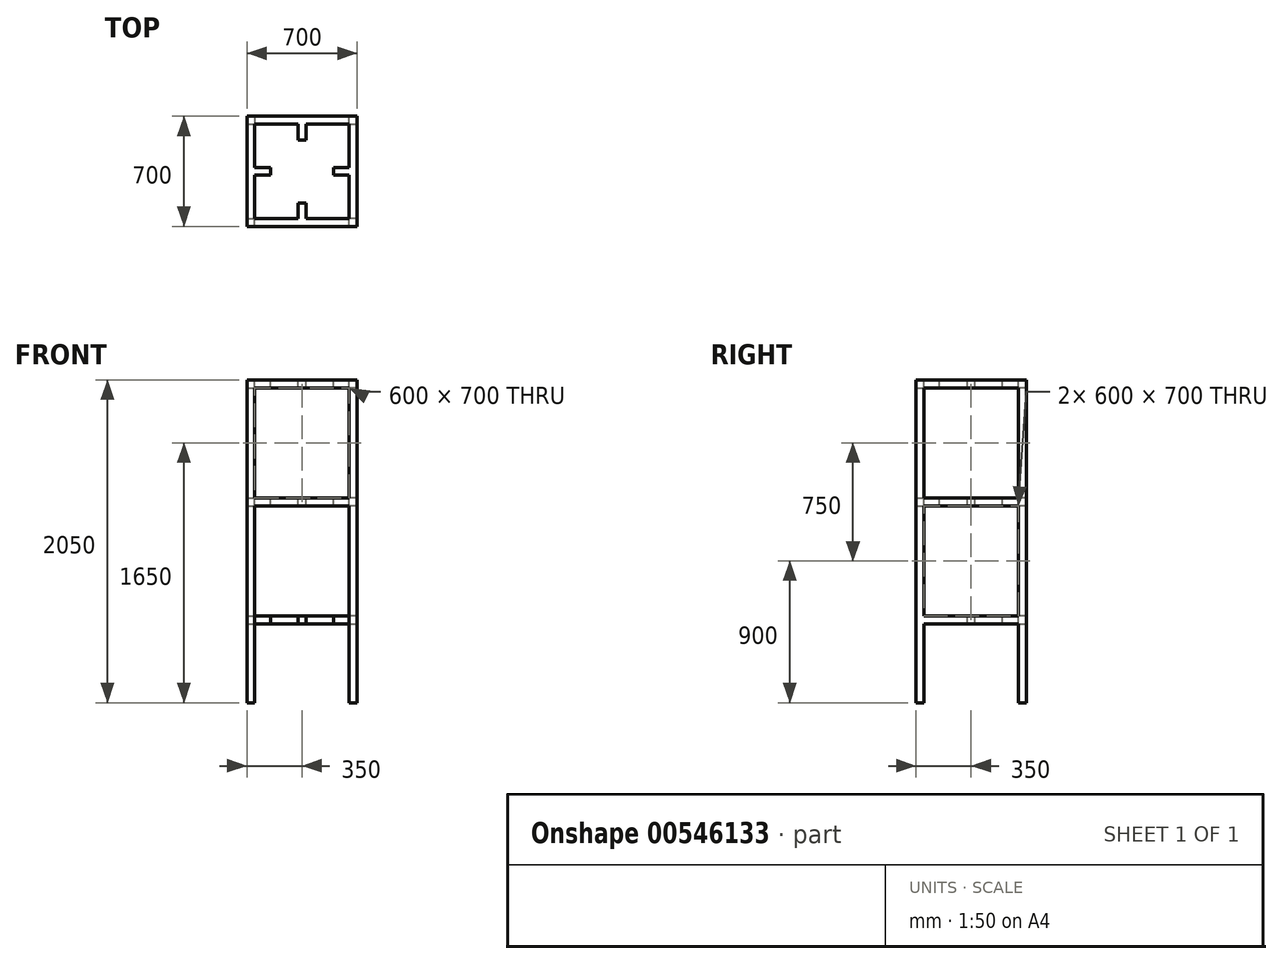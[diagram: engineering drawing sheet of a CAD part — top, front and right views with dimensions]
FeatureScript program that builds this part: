
annotation { "Feature Type Name" : "Feature", "Feature Type Description" : "" }
export const myFeature = defineFeature(function(context is Context, id is Id, definition is map)
    precondition{}
    {
        {
            var Q0;
            Q0=qCreatedBy(makeId("Top.planeOp"),FACE);
            var sketch = newSketch(context, id + "F0", { "sketchPlane" : qUnion([Q0])});
            skLineSegment(sketch, "E0.bottom", {"start": v(350, -350) * mm, "end": v(-350, -350) * mm});
            skLineSegment(sketch, "E0.top", {"start": v(350, 350) * mm, "end": v(-350, 350) * mm});
            skLineSegment(sketch, "E0.left", {"start": v(350, -350) * mm, "end": v(350, 350) * mm});
            skLineSegment(sketch, "E0.right", {"start": v(-350, -350) * mm, "end": v(-350, 350) * mm});
            skPoint(sketch, "E0.middle", {"position": v(0, 0) * mm});
            skLineSegment(sketch, "E1.bottom", {"start": v(300, -300) * mm, "end": v(-300, -300) * mm});
            skLineSegment(sketch, "E1.top", {"start": v(300, 300) * mm, "end": v(-300, 300) * mm});
            skLineSegment(sketch, "E1.left", {"start": v(300, -300) * mm, "end": v(300, 300) * mm});
            skLineSegment(sketch, "E1.right", {"start": v(-300, -300) * mm, "end": v(-300, 300) * mm});
            skSolve(sketch);
        }
        {
            var Q0;
            Q0 = qSketchRegion(id + "F0", true);
            extrude(context, id + "F1", {"entities" : qUnion([Q0]), "oppositeDirection" : true, "depth" : 50 * mm, "offsetDistance" : 25 * mm});
        }
        {
            var Q0;
            Q0=makeQuery(id+"F1.opExtrude","CAP_FACE",FACE,{"disambiguationData":[OSD([sQuery(id+"F0.wireOp",EDGE,"E0.bottom"),sQuery(id+"F0.wireOp",EDGE,"E0.top"),sQuery(id+"F0.wireOp",EDGE,"E0.left"),sQuery(id+"F0.wireOp",EDGE,"E0.right"),sQuery(id+"F0.wireOp",EDGE,"E1.bottom"),sQuery(id+"F0.wireOp",EDGE,"E1.top"),sQuery(id+"F0.wireOp",EDGE,"E1.left"),sQuery(id+"F0.wireOp",EDGE,"E1.right")])],"isStart":false});
            var sketch = newSketch(context, id + "F2", { "sketchPlane" : qUnion([Q0])});
            skLineSegment(sketch, "E2.bottom", {"start": v(-350, 350) * mm, "end": v(-300, 350) * mm});
            skLineSegment(sketch, "E2.top", {"start": v(-350, 300) * mm, "end": v(-300, 300) * mm});
            skLineSegment(sketch, "E2.left", {"start": v(-350, 350) * mm, "end": v(-350, 300) * mm});
            skLineSegment(sketch, "E2.right", {"start": v(-300, 350) * mm, "end": v(-300, 300) * mm});
            skLineSegment(sketch, "E3.bottom", {"start": v(350, 350) * mm, "end": v(300, 350) * mm});
            skLineSegment(sketch, "E3.top", {"start": v(350, 300) * mm, "end": v(300, 300) * mm});
            skLineSegment(sketch, "E3.left", {"start": v(350, 350) * mm, "end": v(350, 300) * mm});
            skLineSegment(sketch, "E3.right", {"start": v(300, 350) * mm, "end": v(300, 300) * mm});
            skLineSegment(sketch, "E4.bottom", {"start": v(350, -350) * mm, "end": v(300, -350) * mm});
            skLineSegment(sketch, "E4.top", {"start": v(350, -300) * mm, "end": v(300, -300) * mm});
            skLineSegment(sketch, "E4.left", {"start": v(350, -350) * mm, "end": v(350, -300) * mm});
            skLineSegment(sketch, "E4.right", {"start": v(300, -350) * mm, "end": v(300, -300) * mm});
            skLineSegment(sketch, "E5.bottom", {"start": v(-350, -350) * mm, "end": v(-300, -350) * mm});
            skLineSegment(sketch, "E5.top", {"start": v(-350, -300) * mm, "end": v(-300, -300) * mm});
            skLineSegment(sketch, "E5.left", {"start": v(-350, -350) * mm, "end": v(-350, -300) * mm});
            skLineSegment(sketch, "E5.right", {"start": v(-300, -350) * mm, "end": v(-300, -300) * mm});
            skSolve(sketch);
        }
        {
            var Q0;
            Q0 = qSketchRegion(id + "F2", true);
            extrude(context, id + "F3", {"entities" : qUnion([Q0]), "operationType" : NewBodyOperationType.ADD, "depth" : 700 * mm, "offsetDistance" : 25 * mm});
        }
        {
            var Q0;
            Q0=makeQuery(id+"F3.opExtrude","CAP_FACE",FACE,{"disambiguationData":[OSD([sQuery(id+"F2.wireOp",EDGE,"E2.bottom"),sQuery(id+"F2.wireOp",EDGE,"E2.top"),sQuery(id+"F2.wireOp",EDGE,"E2.left"),sQuery(id+"F2.wireOp",EDGE,"E2.right")])],"isStart":false});
            var sketch = newSketch(context, id + "F4", { "sketchPlane" : qUnion([Q0])});
            skLineSegment(sketch, "E6.bottom", {"start": v(-350, 350) * mm, "end": v(350, 350) * mm});
            skLineSegment(sketch, "E6.top", {"start": v(-350, -350) * mm, "end": v(350, -350) * mm});
            skLineSegment(sketch, "E6.left", {"start": v(-350, 350) * mm, "end": v(-350, -350) * mm});
            skLineSegment(sketch, "E6.right", {"start": v(350, 350) * mm, "end": v(350, -350) * mm});
            skLineSegment(sketch, "E7.bottom", {"start": v(300, -300) * mm, "end": v(-300, -300) * mm});
            skLineSegment(sketch, "E7.top", {"start": v(300, 300) * mm, "end": v(-300, 300) * mm});
            skLineSegment(sketch, "E7.left", {"start": v(300, -300) * mm, "end": v(300, 300) * mm});
            skLineSegment(sketch, "E7.right", {"start": v(-300, -300) * mm, "end": v(-300, 300) * mm});
            skSolve(sketch);
        }
        {
            var Q0;
            Q0 = qSketchRegion(id + "F4", true);
            extrude(context, id + "F5", {"entities" : qUnion([Q0]), "operationType" : NewBodyOperationType.ADD, "depth" : 50 * mm, "offsetDistance" : 25 * mm});
        }
        {
            var Q0;
            Q0=makeQuery(id+"F1.opExtrude","CAP_FACE",FACE,{"disambiguationData":[OSD([sQuery(id+"F0.wireOp",EDGE,"E0.bottom"),sQuery(id+"F0.wireOp",EDGE,"E0.top"),sQuery(id+"F0.wireOp",EDGE,"E0.left"),sQuery(id+"F0.wireOp",EDGE,"E0.right"),sQuery(id+"F0.wireOp",EDGE,"E1.bottom"),sQuery(id+"F0.wireOp",EDGE,"E1.top"),sQuery(id+"F0.wireOp",EDGE,"E1.left"),sQuery(id+"F0.wireOp",EDGE,"E1.right")])],"isStart":true});
            var sketch = newSketch(context, id + "F6", { "sketchPlane" : qUnion([Q0])});
            skLineSegment(sketch, "E8.bottom", {"start": v(-300, -25) * mm, "end": v(-200, -25) * mm});
            skLineSegment(sketch, "E8.top", {"start": v(-300, 25) * mm, "end": v(-200, 25) * mm});
            skLineSegment(sketch, "E8.left", {"start": v(-300, -25) * mm, "end": v(-300, 25) * mm});
            skLineSegment(sketch, "E8.right", {"start": v(-200, -25) * mm, "end": v(-200, 25) * mm});
            skLineSegment(sketch, "E9.1.0", {"start": v(25, -200) * mm, "end": v(-25, -200) * mm});
            skLineSegment(sketch, "E9.1.1", {"start": v(25, -300) * mm, "end": v(-25, -300) * mm});
            skLineSegment(sketch, "E9.1.2", {"start": v(-25, -300) * mm, "end": v(-25, -200) * mm});
            skLineSegment(sketch, "E9.1.3", {"start": v(25, -300) * mm, "end": v(25, -200) * mm});
            skLineSegment(sketch, "E9.2.0", {"start": v(200, 25) * mm, "end": v(200, -25) * mm});
            skLineSegment(sketch, "E9.2.1", {"start": v(300, 25) * mm, "end": v(300, -25) * mm});
            skLineSegment(sketch, "E9.2.2", {"start": v(300, -25) * mm, "end": v(200, -25) * mm});
            skLineSegment(sketch, "E9.2.3", {"start": v(300, 25) * mm, "end": v(200, 25) * mm});
            skLineSegment(sketch, "E9.3.0", {"start": v(-25, 200) * mm, "end": v(25, 200) * mm});
            skLineSegment(sketch, "E9.3.1", {"start": v(-25, 300) * mm, "end": v(25, 300) * mm});
            skLineSegment(sketch, "E9.3.2", {"start": v(25, 300) * mm, "end": v(25, 200) * mm});
            skLineSegment(sketch, "E9.3.3", {"start": v(-25, 300) * mm, "end": v(-25, 200) * mm});
            skPoint(sketch, "E9.center", {"position": v(0, 0) * mm});
            skSolve(sketch);
        }
        {
            var Q0;
            Q0 = qSketchRegion(id + "F6", true);
            extrude(context, id + "F7", {"entities" : qUnion([Q0]), "operationType" : NewBodyOperationType.ADD, "oppositeDirection" : true, "depth" : 50 * mm, "offsetDistance" : 25 * mm});
        }
        {
            var Q0;
            Q0=makeQuery(id+"F5.opExtrude","CAP_FACE",FACE,{"disambiguationData":[OSD([sQuery(id+"F4.wireOp",EDGE,"E6.bottom"),sQuery(id+"F4.wireOp",EDGE,"E6.top"),sQuery(id+"F4.wireOp",EDGE,"E6.left"),sQuery(id+"F4.wireOp",EDGE,"E6.right"),sQuery(id+"F4.wireOp",EDGE,"E7.bottom"),sQuery(id+"F4.wireOp",EDGE,"E7.top"),sQuery(id+"F4.wireOp",EDGE,"E7.left"),sQuery(id+"F4.wireOp",EDGE,"E7.right")])],"isStart":false});
            var sketch = newSketch(context, id + "F8", { "sketchPlane" : qUnion([Q0])});
            skLineSegment(sketch, "E10.bottom", {"start": v(-350, 350) * mm, "end": v(-300, 350) * mm});
            skLineSegment(sketch, "E10.top", {"start": v(-350, 300) * mm, "end": v(-300, 300) * mm});
            skLineSegment(sketch, "E10.left", {"start": v(-350, 350) * mm, "end": v(-350, 300) * mm});
            skLineSegment(sketch, "E10.right", {"start": v(-300, 350) * mm, "end": v(-300, 300) * mm});
            skLineSegment(sketch, "E11.bottom", {"start": v(350, 350) * mm, "end": v(300, 350) * mm});
            skLineSegment(sketch, "E11.top", {"start": v(350, 300) * mm, "end": v(300, 300) * mm});
            skLineSegment(sketch, "E11.left", {"start": v(350, 350) * mm, "end": v(350, 300) * mm});
            skLineSegment(sketch, "E11.right", {"start": v(300, 350) * mm, "end": v(300, 300) * mm});
            skLineSegment(sketch, "E12.bottom", {"start": v(-350, -350) * mm, "end": v(-300, -350) * mm});
            skLineSegment(sketch, "E12.top", {"start": v(-350, -300) * mm, "end": v(-300, -300) * mm});
            skLineSegment(sketch, "E12.left", {"start": v(-350, -350) * mm, "end": v(-350, -300) * mm});
            skLineSegment(sketch, "E12.right", {"start": v(-300, -350) * mm, "end": v(-300, -300) * mm});
            skLineSegment(sketch, "E13.bottom", {"start": v(350, -350) * mm, "end": v(300, -350) * mm});
            skLineSegment(sketch, "E13.top", {"start": v(350, -300) * mm, "end": v(300, -300) * mm});
            skLineSegment(sketch, "E13.left", {"start": v(350, -350) * mm, "end": v(350, -300) * mm});
            skLineSegment(sketch, "E13.right", {"start": v(300, -350) * mm, "end": v(300, -300) * mm});
            skSolve(sketch);
        }
        {
            var Q0;
            Q0 = qSketchRegion(id + "F8", true);
            extrude(context, id + "F9", {"entities" : qUnion([Q0]), "operationType" : NewBodyOperationType.ADD, "depth" : 700 * mm, "offsetDistance" : 25 * mm});
        }
        {
            var Q0;
            Q0=makeQuery(id+"F9.opExtrude","CAP_FACE",FACE,{"disambiguationData":[OSD([sQuery(id+"F8.wireOp",EDGE,"E11.bottom"),sQuery(id+"F8.wireOp",EDGE,"E11.top"),sQuery(id+"F8.wireOp",EDGE,"E11.left"),sQuery(id+"F8.wireOp",EDGE,"E11.right")])],"isStart":false});
            var sketch = newSketch(context, id + "F10", { "sketchPlane" : qUnion([Q0])});
            skLineSegment(sketch, "E14.bottom", {"start": v(-350, 350) * mm, "end": v(350, 350) * mm});
            skLineSegment(sketch, "E14.top", {"start": v(-350, -350) * mm, "end": v(350, -350) * mm});
            skLineSegment(sketch, "E14.left", {"start": v(-350, 350) * mm, "end": v(-350, -350) * mm});
            skLineSegment(sketch, "E14.right", {"start": v(350, 350) * mm, "end": v(350, -350) * mm});
            skLineSegment(sketch, "E15.bottom", {"start": v(-300, 300) * mm, "end": v(300, 300) * mm});
            skLineSegment(sketch, "E15.top", {"start": v(-300, -300) * mm, "end": v(300, -300) * mm});
            skLineSegment(sketch, "E15.left", {"start": v(-300, 300) * mm, "end": v(-300, -300) * mm});
            skLineSegment(sketch, "E15.right", {"start": v(300, 300) * mm, "end": v(300, -300) * mm});
            skSolve(sketch);
        }
        {
            var Q0;
            Q0 = qSketchRegion(id + "F10", true);
            extrude(context, id + "F11", {"entities" : qUnion([Q0]), "operationType" : NewBodyOperationType.ADD, "depth" : 50 * mm, "offsetDistance" : 25 * mm});
        }
        {
            var Q0;
            Q0=makeQuery(id+"F11.opExtrude","CAP_FACE",FACE,{"disambiguationData":[OSD([sQuery(id+"F10.wireOp",EDGE,"E14.bottom"),sQuery(id+"F10.wireOp",EDGE,"E14.top"),sQuery(id+"F10.wireOp",EDGE,"E14.left"),sQuery(id+"F10.wireOp",EDGE,"E14.right"),sQuery(id+"F10.wireOp",EDGE,"E15.bottom"),sQuery(id+"F10.wireOp",EDGE,"E15.top"),sQuery(id+"F10.wireOp",EDGE,"E15.left"),sQuery(id+"F10.wireOp",EDGE,"E15.right")])],"isStart":false});
            var sketch = newSketch(context, id + "F12", { "sketchPlane" : qUnion([Q0])});
            skLineSegment(sketch, "E16.bottom", {"start": v(-350, 350) * mm, "end": v(-300, 350) * mm});
            skLineSegment(sketch, "E16.top", {"start": v(-350, 300) * mm, "end": v(-300, 300) * mm});
            skLineSegment(sketch, "E16.left", {"start": v(-350, 350) * mm, "end": v(-350, 300) * mm});
            skLineSegment(sketch, "E16.right", {"start": v(-300, 350) * mm, "end": v(-300, 300) * mm});
            skLineSegment(sketch, "E17.bottom", {"start": v(350, 350) * mm, "end": v(300, 350) * mm});
            skLineSegment(sketch, "E17.top", {"start": v(350, 300) * mm, "end": v(300, 300) * mm});
            skLineSegment(sketch, "E17.left", {"start": v(350, 350) * mm, "end": v(350, 300) * mm});
            skLineSegment(sketch, "E17.right", {"start": v(300, 350) * mm, "end": v(300, 300) * mm});
            skLineSegment(sketch, "E18.bottom", {"start": v(-350, -350) * mm, "end": v(-300, -350) * mm});
            skLineSegment(sketch, "E18.top", {"start": v(-350, -300) * mm, "end": v(-300, -300) * mm});
            skLineSegment(sketch, "E18.left", {"start": v(-350, -350) * mm, "end": v(-350, -300) * mm});
            skLineSegment(sketch, "E18.right", {"start": v(-300, -350) * mm, "end": v(-300, -300) * mm});
            skLineSegment(sketch, "E19.bottom", {"start": v(300, -300) * mm, "end": v(350, -300) * mm});
            skLineSegment(sketch, "E19.top", {"start": v(300, -350) * mm, "end": v(350, -350) * mm});
            skLineSegment(sketch, "E19.left", {"start": v(300, -300) * mm, "end": v(300, -350) * mm});
            skLineSegment(sketch, "E19.right", {"start": v(350, -300) * mm, "end": v(350, -350) * mm});
            skSolve(sketch);
        }
        {
            var Q0;
            Q0 = qSketchRegion(id + "F12", true);
            extrude(context, id + "F13", {"entities" : qUnion([Q0]), "operationType" : NewBodyOperationType.ADD, "depth" : 500 * mm, "offsetDistance" : 25 * mm});
        }
        {
            var Q0;
            {var subQ0=sQuery(id+"F4.wireOp",EDGE,"E6.left");var subQ1=sQuery(id+"F4.wireOp",EDGE,"E7.right");var subQ2=sQuery(id+"F4.wireOp",EDGE,"E7.top");var subQ3=sQuery(id+"F4.wireOp",EDGE,"E7.bottom");var subQ4=makeQuery(id+"F5.opExtrude","CAP_FACE",FACE,{"disambiguationData":[OSD([sQuery(id+"F4.wireOp",EDGE,"E6.bottom"),sQuery(id+"F4.wireOp",EDGE,"E6.top"),subQ0,sQuery(id+"F4.wireOp",EDGE,"E6.right"),subQ3,subQ2,sQuery(id+"F4.wireOp",EDGE,"E7.left"),subQ1])],"isStart":true});Q0=makeQuery(id+"F5.boolean.opBoolean","SPLIT",FACE,{"disambiguationData":[TD([makeQuery(id+"F1.opExtrude","SWEPT_FACE",FACE,{"disambiguationData":[OSD([sQuery(id+"F0.wireOp",EDGE,"E0.right")])]})])],"derivedFrom":subQ4});}
            var sketch = newSketch(context, id + "F14", { "sketchPlane" : qUnion([Q0])});
            skLineSegment(sketch, "E20.bottom", {"start": v(-200, 25) * mm, "end": v(-300, 25) * mm});
            skLineSegment(sketch, "E20.top", {"start": v(-200, -25) * mm, "end": v(-300, -25) * mm});
            skLineSegment(sketch, "E20.left", {"start": v(-200, 25) * mm, "end": v(-200, -25) * mm});
            skLineSegment(sketch, "E20.right", {"start": v(-300, 25) * mm, "end": v(-300, -25) * mm});
            skLineSegment(sketch, "E21.1.0", {"start": v(25, -200) * mm, "end": v(25, -300) * mm});
            skLineSegment(sketch, "E21.1.1", {"start": v(-25, -200) * mm, "end": v(-25, -300) * mm});
            skLineSegment(sketch, "E21.1.2", {"start": v(-25, -200) * mm, "end": v(25, -200) * mm});
            skLineSegment(sketch, "E21.1.3", {"start": v(-25, -300) * mm, "end": v(25, -300) * mm});
            skLineSegment(sketch, "E21.2.0", {"start": v(200, 25) * mm, "end": v(300, 25) * mm});
            skLineSegment(sketch, "E21.2.1", {"start": v(200, -25) * mm, "end": v(300, -25) * mm});
            skLineSegment(sketch, "E21.2.2", {"start": v(200, -25) * mm, "end": v(200, 25) * mm});
            skLineSegment(sketch, "E21.2.3", {"start": v(300, -25) * mm, "end": v(300, 25) * mm});
            skLineSegment(sketch, "E21.3.0", {"start": v(-25, 200) * mm, "end": v(-25, 300) * mm});
            skLineSegment(sketch, "E21.3.1", {"start": v(25, 200) * mm, "end": v(25, 300) * mm});
            skLineSegment(sketch, "E21.3.2", {"start": v(25, 200) * mm, "end": v(-25, 200) * mm});
            skLineSegment(sketch, "E21.3.3", {"start": v(25, 300) * mm, "end": v(-25, 300) * mm});
            skPoint(sketch, "E21.center", {"position": v(0, 0) * mm});
            skSolve(sketch);
        }
        {
            var Q0;
            Q0 = qSketchRegion(id + "F14", true);
            extrude(context, id + "F15", {"entities" : qUnion([Q0]), "operationType" : NewBodyOperationType.ADD, "oppositeDirection" : true, "depth" : 50 * mm, "offsetDistance" : 25 * mm});
        }
        {
            var Q0;
            {var subQ0=sQuery(id+"F10.wireOp",EDGE,"E14.bottom");var subQ1=sQuery(id+"F10.wireOp",EDGE,"E15.right");var subQ2=sQuery(id+"F10.wireOp",EDGE,"E15.left");var subQ3=sQuery(id+"F10.wireOp",EDGE,"E15.bottom");var subQ4=makeQuery(id+"F11.opExtrude","CAP_FACE",FACE,{"disambiguationData":[OSD([subQ0,sQuery(id+"F10.wireOp",EDGE,"E14.top"),sQuery(id+"F10.wireOp",EDGE,"E14.left"),sQuery(id+"F10.wireOp",EDGE,"E14.right"),subQ3,sQuery(id+"F10.wireOp",EDGE,"E15.top"),subQ2,subQ1])],"isStart":true});Q0=makeQuery(id+"F11.boolean.opBoolean","SPLIT",FACE,{"disambiguationData":[TD([makeQuery(id+"F1.opExtrude","SWEPT_FACE",FACE,{"disambiguationData":[OSD([sQuery(id+"F0.wireOp",EDGE,"E0.bottom")])]})])],"derivedFrom":subQ4});}
            var sketch = newSketch(context, id + "F16", { "sketchPlane" : qUnion([Q0])});
            skLineSegment(sketch, "E22.bottom", {"start": v(-300, -300) * mm, "end": v(300, -300) * mm});
            skLineSegment(sketch, "E22.top", {"start": v(-300, -350) * mm, "end": v(300, -350) * mm});
            skLineSegment(sketch, "E22.left", {"start": v(-300, -300) * mm, "end": v(-300, -350) * mm});
            skLineSegment(sketch, "E22.right", {"start": v(300, -300) * mm, "end": v(300, -350) * mm});
            skSolve(sketch);
        }
        {
            var Q0;
            Q0 = qSketchRegion(id + "F16", true);
            extrude(context, id + "F17", {"entities" : qUnion([Q0]), "operationType" : NewBodyOperationType.REMOVE, "endBound" : BoundingType.UP_TO_NEXT, "oppositeDirection" : true, "depth" : 50 * mm, "offsetDistance" : 25 * mm});
        }
        {
            var Q0;
            {var subQ0=sQuery(id+"F10.wireOp",EDGE,"E14.left");var subQ1=sQuery(id+"F10.wireOp",EDGE,"E15.left");var subQ2=sQuery(id+"F10.wireOp",EDGE,"E15.top");var subQ3=sQuery(id+"F10.wireOp",EDGE,"E15.bottom");var subQ4=makeQuery(id+"F11.opExtrude","CAP_FACE",FACE,{"disambiguationData":[OSD([sQuery(id+"F10.wireOp",EDGE,"E14.bottom"),sQuery(id+"F10.wireOp",EDGE,"E14.top"),subQ0,sQuery(id+"F10.wireOp",EDGE,"E14.right"),subQ3,subQ2,subQ1,sQuery(id+"F10.wireOp",EDGE,"E15.right")])],"isStart":true});Q0=makeQuery(id+"F11.boolean.opBoolean","SPLIT",FACE,{"disambiguationData":[TD([makeQuery(id+"F1.opExtrude","SWEPT_FACE",FACE,{"disambiguationData":[OSD([sQuery(id+"F0.wireOp",EDGE,"E0.right")])]})])],"derivedFrom":subQ4});}
            var sketch = newSketch(context, id + "F18", { "sketchPlane" : qUnion([Q0])});
            skLineSegment(sketch, "E23.bottom", {"start": v(-200, 25) * mm, "end": v(-300, 25) * mm});
            skLineSegment(sketch, "E23.top", {"start": v(-200, -25) * mm, "end": v(-300, -25) * mm});
            skLineSegment(sketch, "E23.left", {"start": v(-200, 25) * mm, "end": v(-200, -25) * mm});
            skLineSegment(sketch, "E23.right", {"start": v(-300, 25) * mm, "end": v(-300, -25) * mm});
            skLineSegment(sketch, "E24.2.0", {"start": v(200, 25) * mm, "end": v(300, 25) * mm});
            skLineSegment(sketch, "E24.2.1", {"start": v(200, -25) * mm, "end": v(200, 25) * mm});
            skLineSegment(sketch, "E24.2.2", {"start": v(300, -25) * mm, "end": v(300, 25) * mm});
            skLineSegment(sketch, "E24.2.3", {"start": v(200, -25) * mm, "end": v(300, -25) * mm});
            skLineSegment(sketch, "E24.3.0", {"start": v(-25, 200) * mm, "end": v(-25, 300) * mm});
            skLineSegment(sketch, "E24.3.1", {"start": v(25, 200) * mm, "end": v(-25, 200) * mm});
            skLineSegment(sketch, "E24.3.2", {"start": v(25, 300) * mm, "end": v(-25, 300) * mm});
            skLineSegment(sketch, "E24.3.3", {"start": v(25, 200) * mm, "end": v(25, 300) * mm});
            skPoint(sketch, "E24.center", {"position": v(0, 0) * mm});
            skSolve(sketch);
        }
        {
            var Q0;
            Q0 = qSketchRegion(id + "F18", true);
            extrude(context, id + "F19", {"entities" : qUnion([Q0]), "operationType" : NewBodyOperationType.ADD, "oppositeDirection" : true, "depth" : 50 * mm, "offsetDistance" : 25 * mm});
        }
    });
